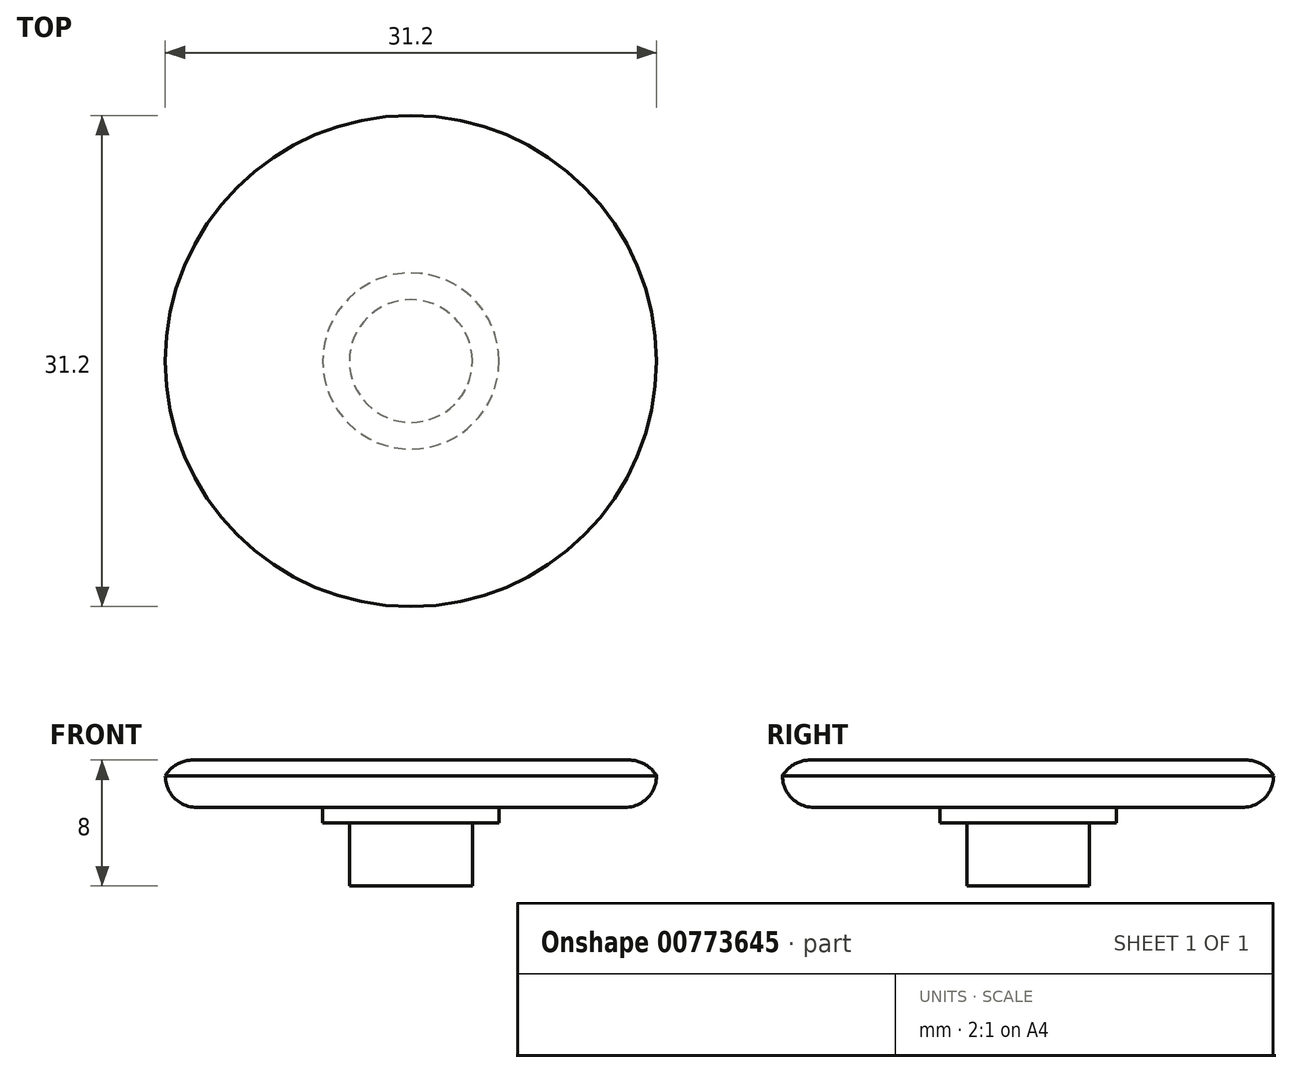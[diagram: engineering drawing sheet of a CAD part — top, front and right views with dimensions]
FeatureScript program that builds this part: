
annotation { "Feature Type Name" : "Feature", "Feature Type Description" : "" }
export const myFeature = defineFeature(function(context is Context, id is Id, definition is map)
    precondition{}
    {
        {
            var Q0;
            Q0=qCreatedBy(makeId("Top.planeOp"),FACE);
            var sketch = newSketch(context, id + "F0", { "sketchPlane" : qUnion([Q0])});
            skCircle(sketch, "E0", {"center": v(0, 0) * mm, "radius": 3.9 * mm});
            skCircle(sketch, "E1", {"center": v(0, 0) * mm, "radius": 5.6 * mm});
            skCircle(sketch, "E2", {"center": v(0, 0) * mm, "radius": 15.6 * mm});
            skSolve(sketch);
        }
        {
            var Q0;
            Q0=makeQuery(id+"F0.imprint","IMPRINT",FACE,{"disambiguationData":[TD([[makeQuery(id+"F0.imprint","IMPRINT",EDGE,{"derivedFrom":sQuery(id+"F0.wireOp",EDGE,"E1")}),-1.0]])]});
            var Q1;
            Q1=makeQuery(id+"F0.imprint","IMPRINT",FACE,{"disambiguationData":[TD([[makeQuery(id+"F0.imprint","IMPRINT",EDGE,{"derivedFrom":sQuery(id+"F0.wireOp",EDGE,"E0")}),-1.0]])]});
            var Q2;
            Q2=makeQuery(id+"F0.imprint","IMPRINT",FACE,{"disambiguationData":[TD([[makeQuery(id+"F0.imprint","IMPRINT",EDGE,{"derivedFrom":sQuery(id+"F0.wireOp",EDGE,"E0")}),1.0]])]});
            extrude(context, id + "F1", {"entities" : qUnion([Q0, Q1, Q2]), "oppositeDirection" : true, "depth" : 3 * mm, "offsetDistance" : 25 * mm});
        }
        {
            var Q0;
            Q0=makeQuery(id+"F0.imprint","IMPRINT",FACE,{"disambiguationData":[TD([[makeQuery(id+"F0.imprint","IMPRINT",EDGE,{"derivedFrom":sQuery(id+"F0.wireOp",EDGE,"E0")}),-1.0]])]});
            var Q1;
            Q1=makeQuery(id+"F0.imprint","IMPRINT",FACE,{"disambiguationData":[TD([[makeQuery(id+"F0.imprint","IMPRINT",EDGE,{"derivedFrom":sQuery(id+"F0.wireOp",EDGE,"E0")}),1.0]])]});
            extrude(context, id + "F2", {"entities" : qUnion([Q0, Q1]), "operationType" : NewBodyOperationType.ADD, "oppositeDirection" : true, "depth" : 4 * mm, "offsetDistance" : 25 * mm});
        }
        {
            var Q0;
            Q0=makeQuery(id+"F0.imprint","IMPRINT",FACE,{"disambiguationData":[TD([[makeQuery(id+"F0.imprint","IMPRINT",EDGE,{"derivedFrom":sQuery(id+"F0.wireOp",EDGE,"E0")}),1.0]])]});
            extrude(context, id + "F3", {"entities" : qUnion([Q0]), "operationType" : NewBodyOperationType.ADD, "oppositeDirection" : true, "depth" : 8 * mm, "offsetDistance" : 25 * mm});
        }
        {
            var Q0;
            Q0=makeQuery(id+"F1.opExtrude","CAP_EDGE",EDGE,{"disambiguationData":[OSD([sQuery(id+"F0.wireOp",EDGE,"E2")])],"isStart":false});
            fillet(context, id + "F4", {"entities" : qUnion([Q0]), "radius" : 2 * mm, "tangentPropagation" : true, "allowEdgeOverflow" : false});
        }
        {
            var Q0;
            Q0=makeQuery(id+"F1.opExtrude","CAP_EDGE",EDGE,{"disambiguationData":[OSD([sQuery(id+"F0.wireOp",EDGE,"E2")])],"isStart":true});
            fillet(context, id + "F5", {"entities" : qUnion([Q0]), "radius" : 2 * mm, "tangentPropagation" : true, "allowEdgeOverflow" : false});
        }
    });
